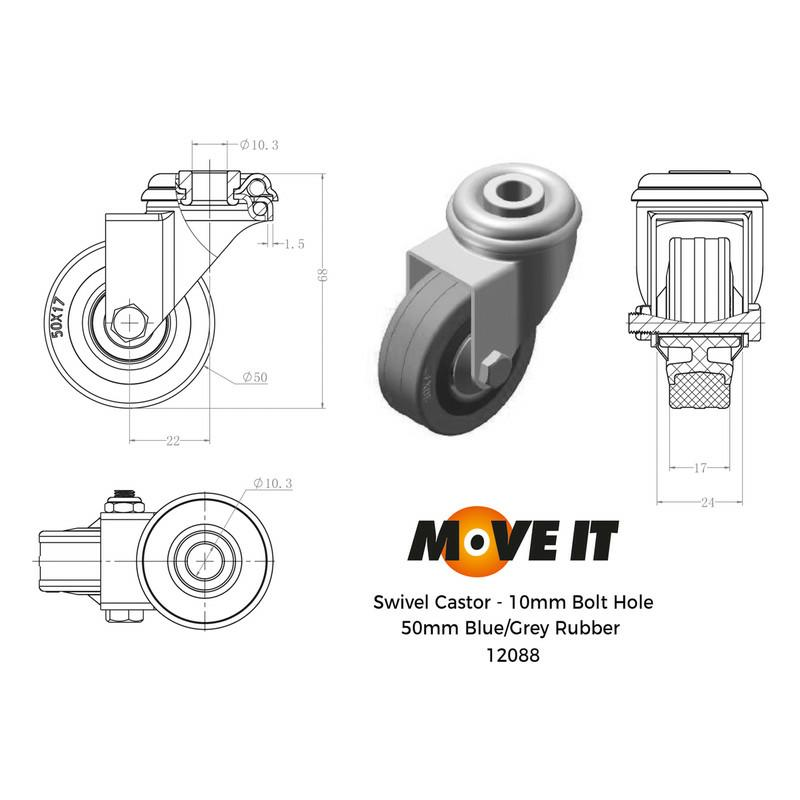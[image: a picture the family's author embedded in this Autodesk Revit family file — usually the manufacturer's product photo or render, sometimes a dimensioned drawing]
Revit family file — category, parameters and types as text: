
# Revit family: Bench
name_source: partatom
category: Generic Models
units: mm (PartAtom-declared; Revit-internal decimal feet)

## family parameters
Always vertical = Yes
Can host rebar = No
Cut with Voids When Loaded = No
Maintain Annotation Orientation = No
Part Type = Normal
Room Calculation Point = No
Round Connector Dimension = Use Diameter
Shared = No
Work Plane-Based = No

## types (1)
- ThinkingWall® Bench
    Base = <By Category>
    Cushion = <By Category>
    Default Elevation = 0 mm  [stored 0 ft]
    Description = Mobile bench with removable padded stools. Part of the ThinkingWall® range for flexible breakout and meeting spaces.
    Manufacturer = Logovisual LTD
    Model = ThinkingWall® Bench
    Plinth = <By Category>
    URL = https://www.logovisual.com

note: [stored X ft] marks values corroborated as IEEE doubles in the binary element streams (Revit-internal decimal feet)

## geometry (parser evidence)
native form markers: Sweep x32
no freeform markers — native parametric forms only
